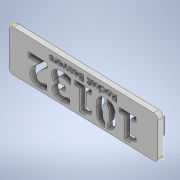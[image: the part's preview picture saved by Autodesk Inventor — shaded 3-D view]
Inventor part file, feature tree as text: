
AUTODESK INVENTOR PART (.ipt)
format: ipt  version: 2020 (Build 240168000, 168)  size: 1,317,376 bytes
history: native  units: in
note: dims shown in document units (in); Inventor stores cm internally (conversion verified against a paired STEP export)
features: other x4, fillet x3, sketch x3, boolean_combine x1
ambient origin geometry x8: Origin, YZ Plane, XZ Plane, XY Plane, X Axis, Y Axis, Z Axis, Center Point
bodies: Solid1 (feature_tree), Solid2 (feature_tree), Solid3 (feature_tree)
feature tree (11):
  other  "Vehicle Registration Plate.iam"
  other  "Vehicle Registration Plate.ipt:1"
  other  "Mount Male.ipt:1"
  other  "Mount Male.ipt:2"
  boolean_combine  "Combine1"
  fillet  "Fillet1"  Radius=0.3937in
  fillet  "Fillet2"  Radius=0.4in
  fillet  "Fillet3"  Radius=0.1in
  sketch  "Sketch6"
  sketch  "Sketch5"
  sketch  "Sketch5_1"  dims[d3=0.2in]
